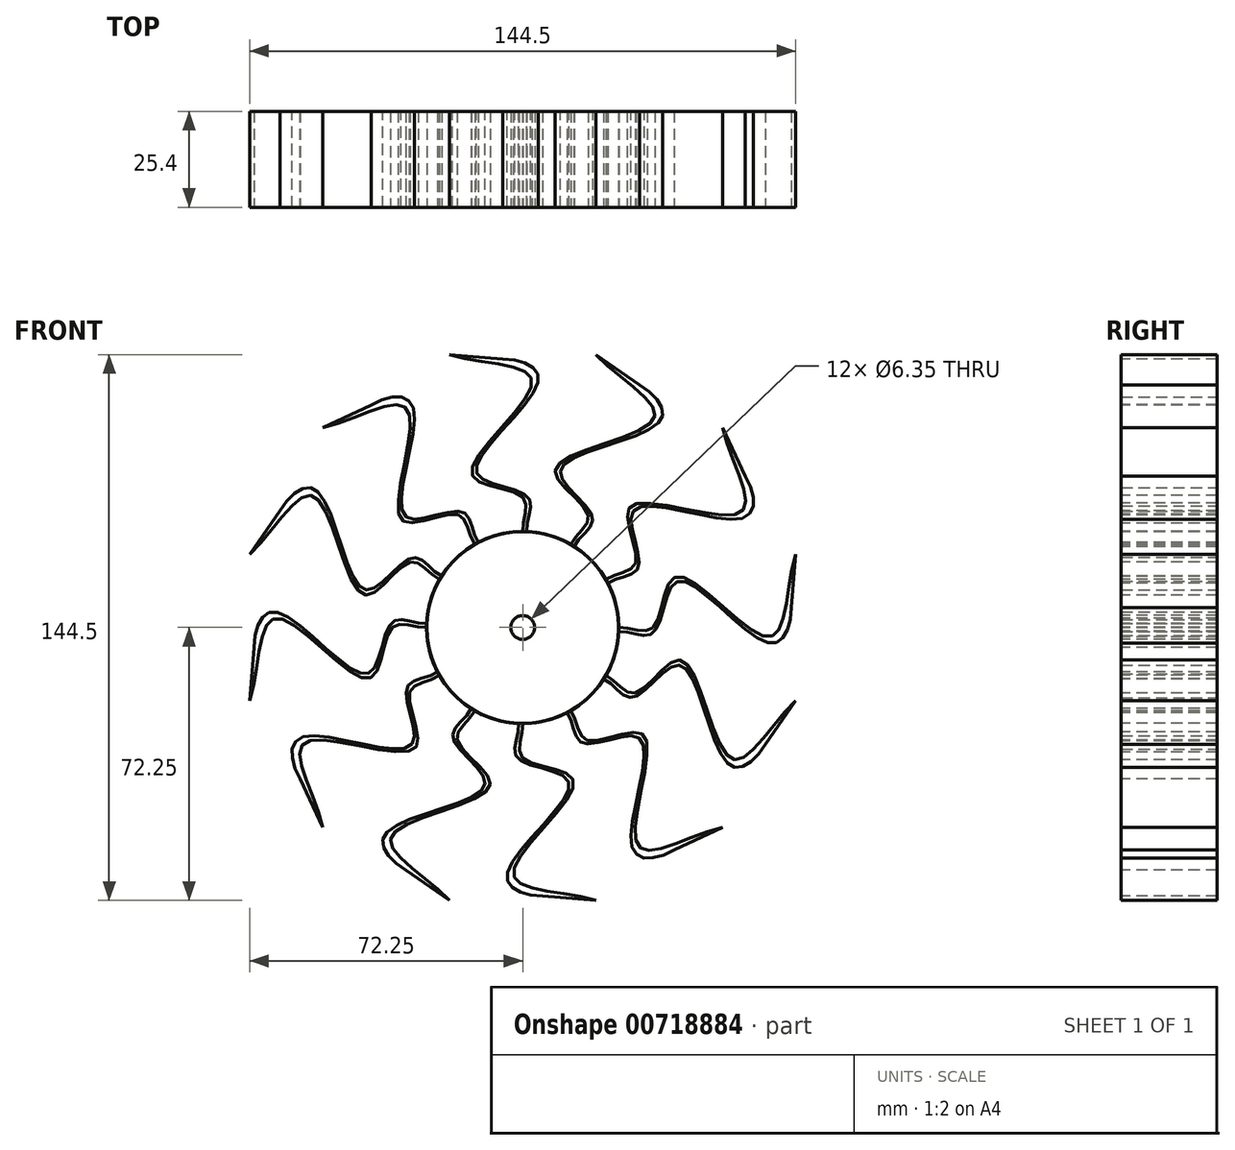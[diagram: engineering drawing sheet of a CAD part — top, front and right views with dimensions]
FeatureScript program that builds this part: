
annotation { "Feature Type Name" : "Feature", "Feature Type Description" : "" }
export const myFeature = defineFeature(function(context is Context, id is Id, definition is map)
    precondition{}
    {
        {
            var Q0;
            Q0=qCreatedBy(makeId("Front.planeOp"),FACE);
            var sketch = newSketch(context, id + "F0", { "sketchPlane" : qUnion([Q0])});
            skCircle(sketch, "E0", {"center": v(0, 0) * mm, "radius": 3.18 * mm});
            skCircle(sketch, "E1", {"center": v(0, 0) * mm, "radius": 25.4 * mm});
            skFitSpline(sketch, "E2", {"points": [v(0, 25.4) * mm, v(0, 34.55) * mm, v(-13.46, 40.75) * mm, v(2.43, 65.04) * mm, v(-19.33, 72.25) * mm], "startDerivative": vector(-3.75, 52.3) * mm, "endDerivative": vector(-85.75, 28.37) * mm});
            skFitSpline(sketch, "E3", {"points": [v(1.07, 25.4) * mm, v(1.4, 34.55) * mm, v(-12.19, 41.14) * mm, v(4.05, 65.04) * mm, v(-5.3, 71) * mm], "startDerivative": vector(-5.27, 49.19) * mm, "endDerivative": vector(-74.6, 0) * mm});
            skLineSegment(sketch, "E4", {"start": v(-5.3, 71) * mm, "end": v(-19.33, 72.25) * mm});
            skLineSegment(sketch, "E5", {"start": v(1.07, 25.38) * mm, "end": v(1.07, 25.4) * mm});
            skLineSegment(sketch, "E6", {"start": v(0, 25.4) * mm, "end": v(1.07, 25.4) * mm});
            skSolve(sketch);
        }
        {
            var Q0;
            Q0 = qSketchRegion(id + "F0", true);
            extrude(context, id + "F1", {"entities" : qUnion([Q0]), "oppositeDirection" : true, "depth" : 25.4 * mm, "offsetDistance" : 25.4 * mm});
        }
        {
            var Q0;
            Q0=makeQuery(id+"F1.opExtrude","SWEPT_BODY",BODY,{"disambiguationData":[OSD([sQuery(id+"F0.wireOp",EDGE,"E0"),sQuery(id+"F0.wireOp",EDGE,"E1"),sQuery(id+"F0.wireOp",EDGE,"E2"),sQuery(id+"F0.wireOp",EDGE,"E3"),sQuery(id+"F0.wireOp",EDGE,"E4"),sQuery(id+"F0.wireOp",EDGE,"E5")])]});
            var Q1;
            Q1=makeQuery(id+"F1.opExtrude","CAP_EDGE",EDGE,{"disambiguationData":[OSD([sQuery(id+"F0.wireOp",EDGE,"E0")])],"isStart":true});
            circularPattern(context, id + "F2", {"entities" : qUnion([Q0]), "axis" : qUnion([Q1]), "angle" : 360 * degree, "instanceCount" : 12, "equalSpace" : true});
        }
    });
